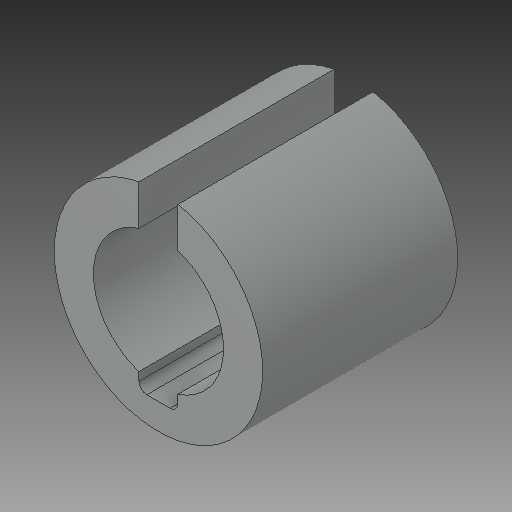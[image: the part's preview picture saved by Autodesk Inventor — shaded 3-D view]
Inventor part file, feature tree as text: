
AUTODESK INVENTOR PART (.ipt)
format: ipt  version: 2018 (Build 220112000, 112)  size: 116,736 bytes
history: native  units: in
note: dims shown in document units (in); Inventor stores cm internally (conversion verified against a paired STEP export)
features: fillet x1
ambient origin geometry x8: Origin, YZ Plane, XZ Plane, XY Plane, X Axis, Y Axis, Z Axis, Center Point
bodies: Solid1 (feature_tree)
feature tree (1):
  fillet  "Fillet1"  [1 undecoded]
note: 1 required parameter value undecoded (feature->parameter linkage not recoverable at this tier; creation-order binding heuristic only, values carry confidence <= 0.55)
